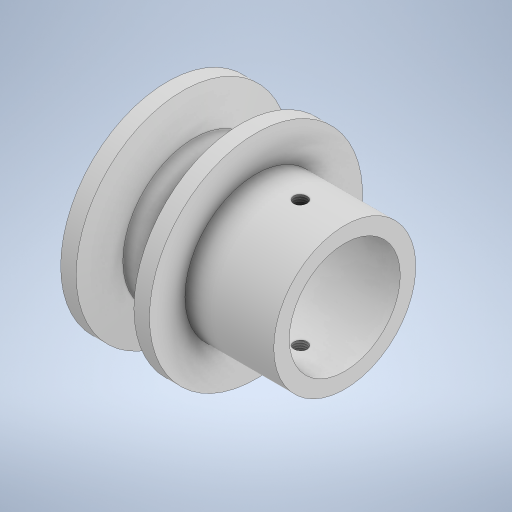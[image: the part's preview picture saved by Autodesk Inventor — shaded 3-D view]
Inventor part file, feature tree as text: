
AUTODESK INVENTOR PART (.ipt)
format: ipt  version: 2023 (Build 270158000, 158)  size: 307,200 bytes
history: native  units: mm
features: sketch x2, revolve x1, extrude x1, thread x1
ambient origin geometry x8: Origin, YZ Plane, XZ Plane, XY Plane, X Axis, Y Axis, Z Axis, Center Point
bodies: Body1 (feature_tree)
feature tree (5):
  sketch  "Эскиз1"
  revolve  "Вращение4"
  extrude  "Выдавливание5"  Depth=24.0mm
  thread  "Резьба4"
  sketch  "Эскиз4"
